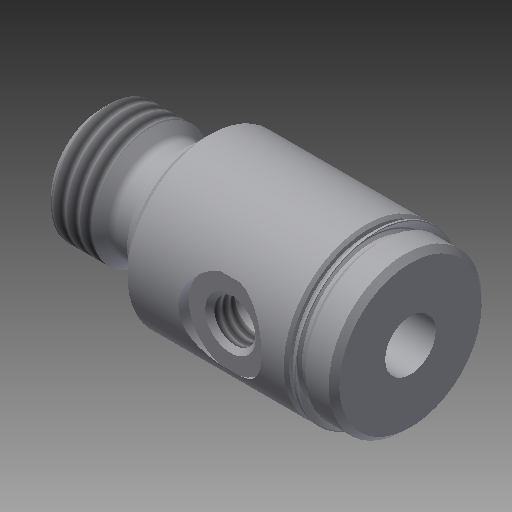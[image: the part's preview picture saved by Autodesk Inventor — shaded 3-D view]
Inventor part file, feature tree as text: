
AUTODESK INVENTOR PART (.ipt)
format: ipt  version: 2018 (Build 220112000, 112)  size: 312,320 bytes
history: native  units: in
note: dims shown in document units (in); Inventor stores cm internally (conversion verified against a paired STEP export)
features: other x119, sketch x5, revolve x4, thread x2, hole x1
ambient origin geometry x8: Origin, YZ Plane, XZ Plane, XY Plane, X Axis, Y Axis, Z Axis, Center Point
bodies: Solid1 (feature_tree)
feature tree (131):
  revolve  "Revolution1"  [1 undecoded]
  thread  "Thread1"  [1 undecoded]
  revolve  "Revolution2"  Angle=360.0deg
  hole  "Hole1"  [1 undecoded]
  revolve  "Revolution3"  [1 undecoded]
  thread  "Thread2"  [1 undecoded]
  revolve  "Revolution4"  [1 undecoded]
  other  "dp1_XY"
  other  "dp1_YZ"
  other  "dp1_ZX"
  other  "dp1_X"
  other  "dp1_Y"
  other  "dp1_Z"
  other  "dp1_Center"
  other  "dp2_XY"
  other  "dp2_YZ"
  other  "dp2_ZX"
  other  "dp2_X"
  other  "dp2_Y"
  other  "dp2_Z"
  other  "dp2_Center"
  other  "hh_XY"
  other  "hh_YZ"
  other  "hh_ZX"
  other  "hh_X"
  other  "hh_Y"
  other  "hh_Z"
  other  "hh_Center"
  other  "port_XY"
  other  "port_YZ"
  other  "port_ZX"
  other  "port_X"
  other  "port_Y"
  other  "port_Z"
  other  "port_Center"
  other  "rod_guide_XY"
  other  "rod_guide_YZ"
  other  "rod_guide_ZX"
  other  "rod_guide_X"
  other  "rod_guide_Y"
  other  "rod_guide_Z"
  other  "rod_guide_Center"
  other  "s1_XY"
  other  "s1_YZ"
  other  "s1_ZX"
  other  "s1_X"
  other  "s1_Y"
  other  "s1_Z"
  other  "s1_Center"
  other  "s2_XY"
  other  "s2_YZ"
  other  "s2_ZX"
  other  "s2_X"
  other  "s2_Y"
  other  "s2_Z"
  other  "s2_Center"
  other  "t1_XY"
  other  "t1_YZ"
  other  "t1_ZX"
  other  "t1_X"
  other  "t1_Y"
  other  "t1_Z"
  other  "t1_Center"
  other  "t111_XY"
  other  "t111_YZ"
  other  "t111_ZX"
  other  "t111_X"
  other  "t111_Y"
  other  "t111_Z"
  other  "t111_Center"
  other  "to_foot_bracket_XY"
  other  "to_foot_bracket_YZ"
  other  "to_foot_bracket_ZX"
  other  "to_foot_bracket_X"
  other  "to_foot_bracket_Y"
  other  "to_foot_bracket_Z"
  other  "to_foot_bracket_Center"
  other  "to_nut_XY"
  other  "to_nut_YZ"
  other  "to_nut_ZX"
  other  "to_nut_X"
  other  "to_nut_Y"
  other  "to_nut_Z"
  other  "to_nut_Center"
  other  "to_rod_XY"
  other  "to_rod_YZ"
  other  "to_rod_ZX"
  other  "to_rod_X"
  other  "to_rod_Y"
  other  "to_rod_Z"
  other  "to_rod_Center"
  other  "to_screw_XY"
  other  "to_screw_YZ"
  other  "to_screw_ZX"
  other  "to_screw_X"
  other  "to_screw_Y"
  other  "to_screw_Z"
  other  "to_screw_Center"
  other  "to_trunnion_brackets_XY"
  other  "to_trunnion_brackets_YZ"
  other  "to_trunnion_brackets_ZX"
  other  "to_trunnion_brackets_X"
  other  "to_trunnion_brackets_Y"
  other  "to_trunnion_brackets_Z"
  other  "to_trunnion_brackets_Center"
  other  "to_trunnion_brackets1_XY"
  other  "to_trunnion_brackets1_YZ"
  other  "to_trunnion_brackets1_ZX"
  other  "to_trunnion_brackets1_X"
  other  "to_trunnion_brackets1_Y"
  other  "to_trunnion_brackets1_Z"
  other  "to_trunnion_brackets1_Center"
  other  "to_trunnion_brackets2_XY"
  other  "to_trunnion_brackets2_YZ"
  other  "to_trunnion_brackets2_ZX"
  other  "to_trunnion_brackets2_X"
  other  "to_trunnion_brackets2_Y"
  other  "to_trunnion_brackets2_Z"
  other  "to_trunnion_brackets2_Center"
  other  "to_tube_XY"
  other  "to_tube_YZ"
  other  "to_tube_ZX"
  other  "to_tube_X"
  other  "to_tube_Y"
  other  "to_tube_Z"
  other  "to_tube_Center"
  sketch  "Sketch_2"  dims[d0=360.0deg d1=0.1537in d2=0.0in d3=360.0deg]
  sketch  "Sketch_3"  dims[d4=0.19in d5=0.75in d6=0.23in d7=0.25in d8=90.0deg d9=1.156in d10=0.0in d11=360.0deg]
  sketch  "Sketch3"  dims[d12=0.0786in d13=0.0in d14=360.0deg]
  sketch  "Sketch_12"  dims[d15=0.0in d16=0.0in d17=0.0in d18=0.0in d19=0.0in d20=0.0in]
  sketch  "Sketch_47"
note: 6 required parameter values undecoded (feature->parameter linkage not recoverable at this tier; creation-order binding heuristic only, values carry confidence <= 0.55)